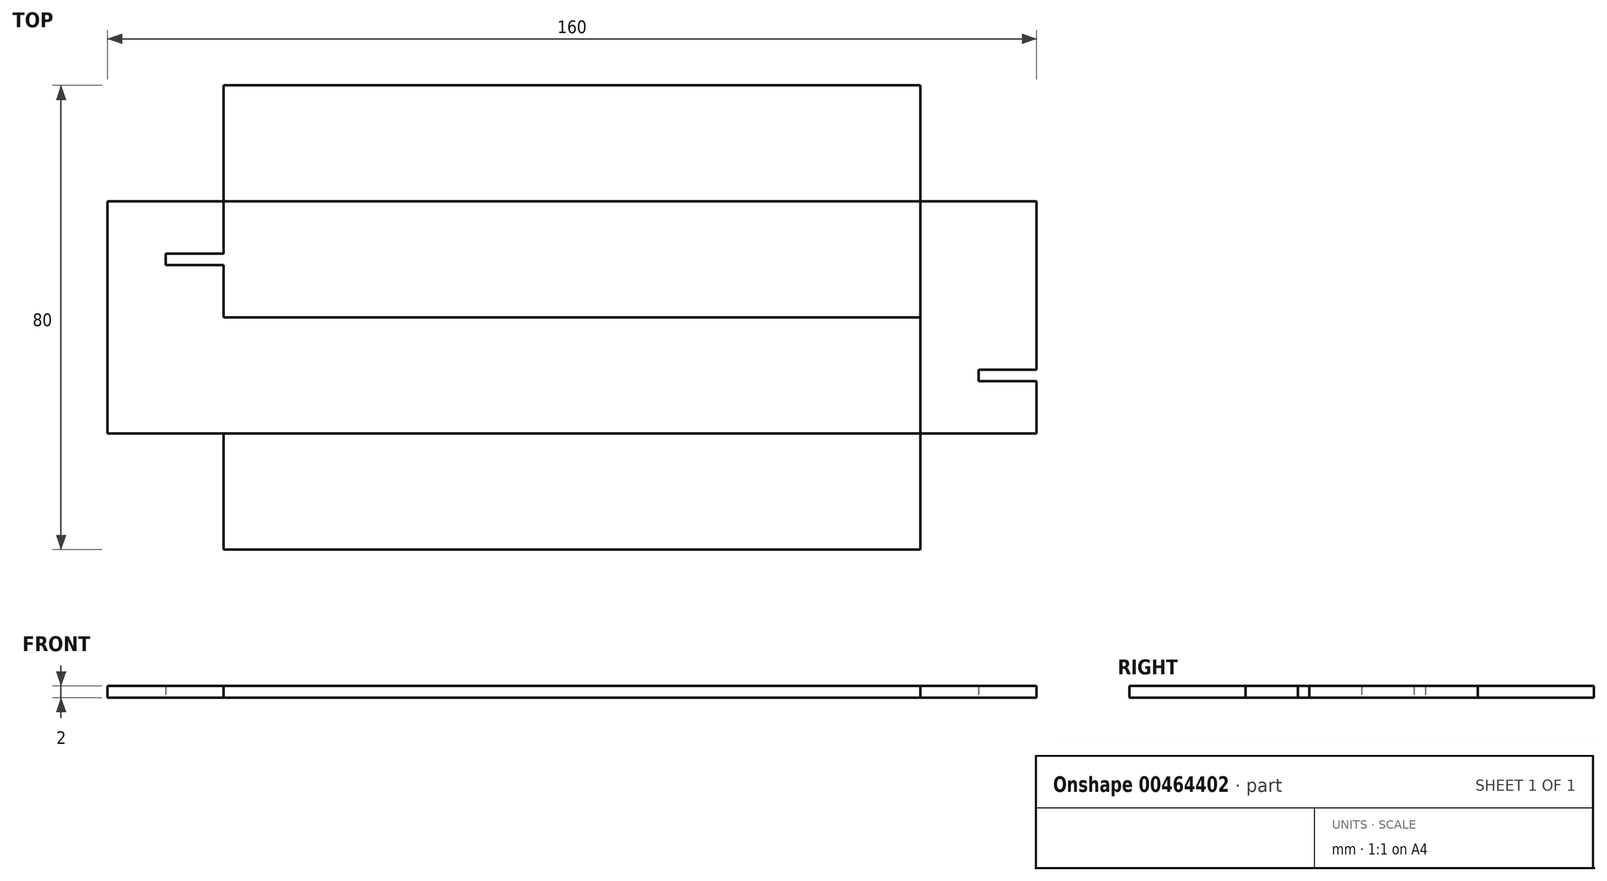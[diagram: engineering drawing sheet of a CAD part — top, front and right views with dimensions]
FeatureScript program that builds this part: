
annotation { "Feature Type Name" : "Feature", "Feature Type Description" : "" }
export const myFeature = defineFeature(function(context is Context, id is Id, definition is map)
    precondition{}
    {
        {
            var Q0;
            Q0=qCreatedBy(makeId("Top.planeOp"),FACE);
            var sketch = newSketch(context, id + "F0", { "sketchPlane" : qUnion([Q0])});
            skLineSegment(sketch, "E0.bottom", {"start": v(-80, 40) * mm, "end": v(80, 40) * mm});
            skLineSegment(sketch, "E0.top", {"start": v(-80, -40) * mm, "end": v(80, -40) * mm});
            skLineSegment(sketch, "E0.left", {"start": v(-80, 40) * mm, "end": v(-80, -40) * mm});
            skLineSegment(sketch, "E0.right", {"start": v(80, 40) * mm, "end": v(80, -40) * mm});
            skPoint(sketch, "E0.middle", {"position": v(0, 0) * mm});
            skLineSegment(sketch, "E1", {"start": v(-80, 0) * mm, "end": v(80, 0) * mm});
            skLineSegment(sketch, "E2", {"start": v(-80, 40) * mm, "end": v(-80, 0) * mm});
            skLineSegment(sketch, "E3", {"start": v(-80, -40) * mm, "end": v(-80, 0) * mm});
            skLineSegment(sketch, "E4", {"start": v(-80, -20) * mm, "end": v(80, -20) * mm});
            skLineSegment(sketch, "E5", {"start": v(-80, 20) * mm, "end": v(80, 20) * mm});
            skLineSegment(sketch, "E6", {"start": v(-80, 40) * mm, "end": v(-60, 40) * mm});
            skLineSegment(sketch, "E7", {"start": v(-60, 40) * mm, "end": v(-60, -40) * mm});
            skLineSegment(sketch, "E8", {"start": v(80, -40) * mm, "end": v(60, -40) * mm});
            skLineSegment(sketch, "E9", {"start": v(60, -40) * mm, "end": v(60, 40) * mm});
            skLineSegment(sketch, "E10.bottom", {"start": v(-60, 11) * mm, "end": v(-70, 11) * mm});
            skLineSegment(sketch, "E10.top", {"start": v(-60, 9) * mm, "end": v(-70, 9) * mm});
            skLineSegment(sketch, "E10.left", {"start": v(-60, 11) * mm, "end": v(-60, 9) * mm});
            skLineSegment(sketch, "E10.right", {"start": v(-70, 11) * mm, "end": v(-70, 9) * mm});
            skLineSegment(sketch, "E11.bottom", {"start": v(80, -9) * mm, "end": v(70, -9) * mm});
            skLineSegment(sketch, "E11.top", {"start": v(80, -11) * mm, "end": v(70, -11) * mm});
            skLineSegment(sketch, "E11.left", {"start": v(80, -9) * mm, "end": v(80, -11) * mm});
            skLineSegment(sketch, "E11.right", {"start": v(70, -9) * mm, "end": v(70, -11) * mm});
            skSolve(sketch);
        }
        {
            var Q0;
            {var subQ0=sQuery(id+"F0.wireOp",EDGE,"E7");var subQ5=sQuery(id+"F0.wireOp",EDGE,"E5");var subQ6=makeQuery(id+"F0.imprint","INTERSECT",VERTEX,{"derivedFrom":[subQ5,subQ0]});Q0=makeQuery(id+"F0.imprint","IMPRINT",FACE,{"disambiguationData":[TD([[makeQuery(id+"F0.imprint","IMPRINT",EDGE,{"disambiguationData":[TD([[subQ6,-1.0]])],"derivedFrom":subQ5}),1.0]])]});}
            var Q1;
            {var subQ0=sQuery(id+"F0.wireOp",EDGE,"E6");Q1=makeQuery(id+"F0.imprint","IMPRINT",FACE,{"disambiguationData":[TD([[makeQuery(id+"F0.imprint","IMPRINT",EDGE,{"derivedFrom":subQ0}),-1.0]])]});}
            var Q2;
            {var subQ6=sQuery(id+"F0.wireOp",EDGE,"E10.bottom");Q2=makeQuery(id+"F0.imprint","IMPRINT",FACE,{"disambiguationData":[TD([[makeQuery(id+"F0.imprint","IMPRINT",EDGE,{"derivedFrom":subQ6}),-1.0]])]});}
            var Q3;
            {var subQ0=sQuery(id+"F0.wireOp",EDGE,"E3");var subQ5=sQuery(id+"F0.wireOp",EDGE,"E4");var subQ6=makeQuery(id+"F0.imprint","INTERSECT",VERTEX,{"derivedFrom":[subQ0,subQ5]});Q3=makeQuery(id+"F0.imprint","IMPRINT",FACE,{"disambiguationData":[TD([[makeQuery(id+"F0.imprint","IMPRINT",EDGE,{"disambiguationData":[TD([[subQ6,-1.0]])],"derivedFrom":subQ5}),1.0]])]});}
            var Q4;
            {var subQ0=sQuery(id+"F0.wireOp",EDGE,"E7");var subQ1=sQuery(id+"F0.wireOp",EDGE,"E1");var subQ2=makeQuery(id+"F0.imprint","INTERSECT",VERTEX,{"derivedFrom":[subQ1,subQ0]});Q4=makeQuery(id+"F0.imprint","IMPRINT",FACE,{"disambiguationData":[TD([[makeQuery(id+"F0.imprint","IMPRINT",EDGE,{"disambiguationData":[TD([[subQ2,-1.0]])],"derivedFrom":subQ1}),-1.0]])]});}
            extrude(context, id + "F1", {"entities" : qUnion([Q0, Q1, Q2, Q3, Q4]), "depth" : 2 * mm});
        }
        {
            var Q0;
            {var subQ0=sQuery(id+"F0.wireOp",EDGE,"E10.left");Q0=makeQuery(id+"F0.imprint","IMPRINT",FACE,{"disambiguationData":[TD([[makeQuery(id+"F0.imprint","IMPRINT",EDGE,{"derivedFrom":subQ0}),1.0]])]});}
            var Q1;
            {var subQ0=sQuery(id+"F0.wireOp",EDGE,"E1");var subQ1=sQuery(id+"F0.wireOp",EDGE,"E0.right");var subQ2=makeQuery(id+"F0.imprint","INTERSECT",VERTEX,{"derivedFrom":[subQ1,subQ0]});Q1=makeQuery(id+"F0.imprint","IMPRINT",FACE,{"disambiguationData":[TD([[makeQuery(id+"F0.imprint","IMPRINT",EDGE,{"disambiguationData":[TD([[subQ2,1.0]])],"derivedFrom":subQ1}),-1.0]])]});}
            var Q2;
            {var subQ10=sQuery(id+"F0.wireOp",EDGE,"E11.bottom");Q2=makeQuery(id+"F0.imprint","IMPRINT",FACE,{"disambiguationData":[TD([[makeQuery(id+"F0.imprint","IMPRINT",EDGE,{"derivedFrom":subQ10}),-1.0]])]});}
            var Q3;
            {var subQ0=sQuery(id+"F0.wireOp",EDGE,"E8");Q3=makeQuery(id+"F0.imprint","IMPRINT",FACE,{"disambiguationData":[TD([[makeQuery(id+"F0.imprint","IMPRINT",EDGE,{"derivedFrom":subQ0}),-1.0]])]});}
            var Q4;
            {var subQ3=sQuery(id+"F0.wireOp",EDGE,"E7");var subQ5=sQuery(id+"F0.wireOp",EDGE,"E4");var subQ6=makeQuery(id+"F0.imprint","INTERSECT",VERTEX,{"derivedFrom":[subQ5,subQ3]});Q4=makeQuery(id+"F0.imprint","IMPRINT",FACE,{"disambiguationData":[TD([[makeQuery(id+"F0.imprint","IMPRINT",EDGE,{"disambiguationData":[TD([[subQ6,-1.0]])],"derivedFrom":subQ5}),-1.0]])]});}
            extrude(context, id + "F2", {"entities" : qUnion([Q0, Q1, Q2, Q3, Q4]), "depth" : 2 * mm});
        }
    });
